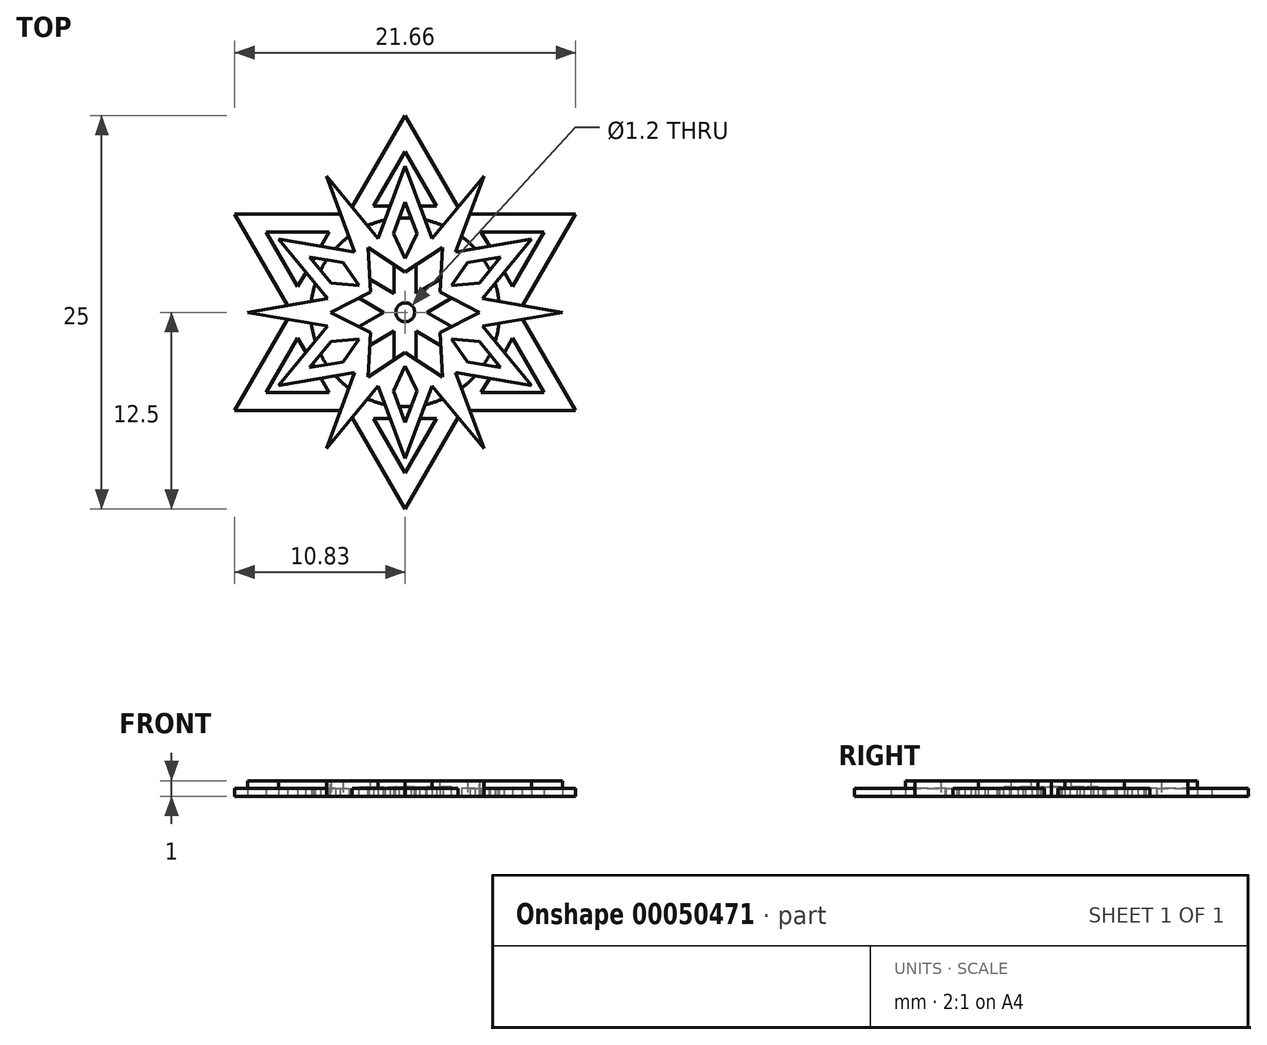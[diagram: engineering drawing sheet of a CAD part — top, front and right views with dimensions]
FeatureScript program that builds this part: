
annotation { "Feature Type Name" : "Feature", "Feature Type Description" : "" }
export const myFeature = defineFeature(function(context is Context, id is Id, definition is map)
    precondition{}
    {
        {
            var Q0;
            Q0=qCreatedBy(makeId("Top.planeOp"),FACE);
            var sketch = newSketch(context, id + "F0", { "sketchPlane" : qUnion([Q0])});
            skCircle(sketch, "E0", {"center": v(0, 0) * mm, "radius": 12.5 * mm, "construction": true});
            skLineSegment(sketch, "E1", {"start": v(0, 12.5) * mm, "end": v(-10.83, -6.25) * mm});
            skLineSegment(sketch, "E2", {"start": v(-10.83, -6.25) * mm, "end": v(10.83, -6.25) * mm});
            skLineSegment(sketch, "E3", {"start": v(10.83, -6.25) * mm, "end": v(0, 12.5) * mm});
            skLineSegment(sketch, "E4", {"start": v(-10.83, 6.25) * mm, "end": v(10.83, 6.25) * mm});
            skLineSegment(sketch, "E5", {"start": v(10.83, 6.25) * mm, "end": v(0, -12.5) * mm});
            skLineSegment(sketch, "E6", {"start": v(0, -12.5) * mm, "end": v(-10.83, 6.25) * mm});
            skCircle(sketch, "E7", {"center": v(0, 0) * mm, "radius": 6 * mm});
            skLineSegment(sketch, "E8", {"start": v(-2, 6.73) * mm, "end": v(2, 6.73) * mm});
            skLineSegment(sketch, "E9", {"start": v(2, 6.73) * mm, "end": v(0, 10.2) * mm});
            skLineSegment(sketch, "E10", {"start": v(0, 10.2) * mm, "end": v(-2, 6.73) * mm});
            skLineSegment(sketch, "E11", {"start": v(0, 10.2) * mm, "end": v(0, 12.5) * mm, "construction": true});
            skLineSegment(sketch, "E12.1.0", {"start": v(-4.83, 5.1) * mm, "end": v(-8.83, 5.1) * mm});
            skLineSegment(sketch, "E12.1.1", {"start": v(-6.83, 1.63) * mm, "end": v(-4.83, 5.1) * mm});
            skLineSegment(sketch, "E12.1.2", {"start": v(-8.83, 5.1) * mm, "end": v(-6.83, 1.63) * mm});
            skLineSegment(sketch, "E12.2.0", {"start": v(-6.83, -1.63) * mm, "end": v(-8.83, -5.1) * mm});
            skLineSegment(sketch, "E12.2.1", {"start": v(-4.83, -5.1) * mm, "end": v(-6.83, -1.63) * mm});
            skLineSegment(sketch, "E12.2.2", {"start": v(-8.83, -5.1) * mm, "end": v(-4.83, -5.1) * mm});
            skLineSegment(sketch, "E12.3.0", {"start": v(-2, -6.73) * mm, "end": v(0, -10.2) * mm});
            skLineSegment(sketch, "E12.3.1", {"start": v(2, -6.73) * mm, "end": v(-2, -6.73) * mm});
            skLineSegment(sketch, "E12.3.2", {"start": v(0, -10.2) * mm, "end": v(2, -6.73) * mm});
            skLineSegment(sketch, "E12.4.0", {"start": v(4.83, -5.1) * mm, "end": v(8.83, -5.1) * mm});
            skLineSegment(sketch, "E12.4.1", {"start": v(6.83, -1.63) * mm, "end": v(4.83, -5.1) * mm});
            skLineSegment(sketch, "E12.4.2", {"start": v(8.83, -5.1) * mm, "end": v(6.83, -1.63) * mm});
            skLineSegment(sketch, "E12.5.0", {"start": v(6.83, 1.63) * mm, "end": v(8.83, 5.1) * mm});
            skLineSegment(sketch, "E12.5.1", {"start": v(4.83, 5.1) * mm, "end": v(6.83, 1.63) * mm});
            skLineSegment(sketch, "E12.5.2", {"start": v(8.83, 5.1) * mm, "end": v(4.83, 5.1) * mm});
            skSolve(sketch);
        }
        {
            var Q0;
            Q0=qSketchRegion(id+"F0",true);
            extrude(context, id + "F1", {"entities" : qUnion([Q0]), "depth" : .5 * mm});
        }
        {
            var Q0;
            Q0=qCreatedBy(makeId("Top.planeOp"),FACE);
            var sketch = newSketch(context, id + "F2", { "sketchPlane" : qUnion([Q0])});
            skArc(sketch, "E13", {"start": v(-1.72, 4.7) * mm, "mid": v(-2.5, 4.33) * mm, "end": v(-3.2, 3.84) * mm});
            skLineSegment(sketch, "E14", {"start": v(-1.72, 4.7) * mm, "end": v(0, 9.28) * mm});
            skLineSegment(sketch, "E15", {"start": v(0, 9.28) * mm, "end": v(1.72, 4.7) * mm});
            skPoint(sketch, "E16.visualSharp", {"position": v(0, 11.28) * mm});
            skPoint(sketch, "E17.orphan", {"position": v(0, 9.28) * mm});
            skLineSegment(sketch, "E18.1.0", {"start": v(-4.93, 0.86) * mm, "end": v(-8.04, 4.64) * mm});
            skLineSegment(sketch, "E18.1.3", {"start": v(-8.04, 4.64) * mm, "end": v(-3.2, 3.84) * mm});
            skLineSegment(sketch, "E18.2.0", {"start": v(-3.2, -3.84) * mm, "end": v(-8.04, -4.64) * mm});
            skLineSegment(sketch, "E18.2.3", {"start": v(-8.04, -4.64) * mm, "end": v(-4.93, -0.86) * mm});
            skLineSegment(sketch, "E18.3.0", {"start": v(1.72, -4.7) * mm, "end": v(0, -9.28) * mm});
            skLineSegment(sketch, "E18.3.3", {"start": v(0, -9.28) * mm, "end": v(-1.72, -4.7) * mm});
            skLineSegment(sketch, "E18.4.0", {"start": v(4.93, -0.86) * mm, "end": v(8.04, -4.64) * mm});
            skLineSegment(sketch, "E18.4.3", {"start": v(8.04, -4.64) * mm, "end": v(3.2, -3.84) * mm});
            skLineSegment(sketch, "E18.5.0", {"start": v(3.2, 3.84) * mm, "end": v(8.04, 4.64) * mm});
            skLineSegment(sketch, "E18.5.3", {"start": v(8.04, 4.64) * mm, "end": v(4.93, 0.86) * mm});
            skArc(sketch, "E19.trimOffspring", {"start": v(3.2, 3.84) * mm, "mid": v(2.5, 4.33) * mm, "end": v(1.72, 4.7) * mm});
            skArc(sketch, "E20.trimOffspring", {"start": v(-4.93, 0.86) * mm, "mid": v(-5, 0) * mm, "end": v(-4.93, -0.86) * mm});
            skArc(sketch, "E21.trimOffspring", {"start": v(4.93, -0.86) * mm, "mid": v(5, 0) * mm, "end": v(4.93, 0.86) * mm});
            skArc(sketch, "E22.trimOffspring", {"start": v(1.72, -4.7) * mm, "mid": v(2.5, -4.33) * mm, "end": v(3.2, -3.84) * mm});
            skArc(sketch, "E23.trimOffspring", {"start": v(-3.2, -3.84) * mm, "mid": v(-2.5, -4.33) * mm, "end": v(-1.72, -4.7) * mm});
            skLineSegment(sketch, "E24", {"start": v(0, 7) * mm, "end": v(0.75, 5) * mm});
            skLineSegment(sketch, "E25", {"start": v(0.75, 5) * mm, "end": v(-0.75, 5) * mm});
            skLineSegment(sketch, "E26", {"start": v(-0.75, 5) * mm, "end": v(0, 7) * mm});
            skLineSegment(sketch, "E27.1.0", {"start": v(-4.7, 1.85) * mm, "end": v(-6.06, 3.5) * mm});
            skLineSegment(sketch, "E27.1.1", {"start": v(-6.06, 3.5) * mm, "end": v(-3.96, 3.15) * mm});
            skLineSegment(sketch, "E27.1.2", {"start": v(-3.96, 3.15) * mm, "end": v(-4.7, 1.85) * mm});
            skLineSegment(sketch, "E27.2.0", {"start": v(-3.96, -3.15) * mm, "end": v(-6.06, -3.5) * mm});
            skLineSegment(sketch, "E27.2.1", {"start": v(-6.06, -3.5) * mm, "end": v(-4.7, -1.85) * mm});
            skLineSegment(sketch, "E27.2.2", {"start": v(-4.7, -1.85) * mm, "end": v(-3.96, -3.15) * mm});
            skLineSegment(sketch, "E27.3.0", {"start": v(0.75, -5) * mm, "end": v(0, -7) * mm});
            skLineSegment(sketch, "E27.3.1", {"start": v(0, -7) * mm, "end": v(-0.75, -5) * mm});
            skLineSegment(sketch, "E27.3.2", {"start": v(-0.75, -5) * mm, "end": v(0.75, -5) * mm});
            skLineSegment(sketch, "E27.4.0", {"start": v(4.7, -1.85) * mm, "end": v(6.06, -3.5) * mm});
            skLineSegment(sketch, "E27.4.1", {"start": v(6.06, -3.5) * mm, "end": v(3.96, -3.15) * mm});
            skLineSegment(sketch, "E27.4.2", {"start": v(3.96, -3.15) * mm, "end": v(4.7, -1.85) * mm});
            skLineSegment(sketch, "E27.5.0", {"start": v(3.96, 3.15) * mm, "end": v(6.06, 3.5) * mm});
            skLineSegment(sketch, "E27.5.1", {"start": v(6.06, 3.5) * mm, "end": v(4.7, 1.85) * mm});
            skLineSegment(sketch, "E27.5.2", {"start": v(4.7, 1.85) * mm, "end": v(3.96, 3.15) * mm});
            skLineSegment(sketch, "E28", {"start": v(0, 9.28) * mm, "end": v(0, 11.28) * mm, "construction": true});
            skLineSegment(sketch, "E29", {"start": v(-3.2, 3.84) * mm, "end": v(-5, 8.66) * mm});
            skLineSegment(sketch, "E30", {"start": v(-5, 8.66) * mm, "end": v(-1.72, 4.7) * mm});
            skLineSegment(sketch, "E31", {"start": v(-5, 8.66) * mm, "end": v(-2.5, 4.33) * mm, "construction": true});
            skLineSegment(sketch, "E32.1.0", {"start": v(-10, 0) * mm, "end": v(-4.93, 0.86) * mm});
            skLineSegment(sketch, "E32.1.1", {"start": v(-4.93, -0.86) * mm, "end": v(-10, 0) * mm});
            skLineSegment(sketch, "E32.2.0", {"start": v(-5, -8.66) * mm, "end": v(-3.2, -3.84) * mm});
            skLineSegment(sketch, "E32.2.1", {"start": v(-1.72, -4.7) * mm, "end": v(-5, -8.66) * mm});
            skLineSegment(sketch, "E32.3.0", {"start": v(5, -8.66) * mm, "end": v(1.72, -4.7) * mm});
            skLineSegment(sketch, "E32.3.1", {"start": v(3.2, -3.84) * mm, "end": v(5, -8.66) * mm});
            skLineSegment(sketch, "E32.4.0", {"start": v(10, 0) * mm, "end": v(4.93, -0.86) * mm});
            skLineSegment(sketch, "E32.4.1", {"start": v(4.93, 0.86) * mm, "end": v(10, 0) * mm});
            skLineSegment(sketch, "E32.5.0", {"start": v(5, 8.66) * mm, "end": v(3.2, 3.84) * mm});
            skLineSegment(sketch, "E32.5.1", {"start": v(1.72, 4.7) * mm, "end": v(5, 8.66) * mm});
            skSolve(sketch);
        }
        {
            var Q0;
            Q0=qSketchRegion(id+"F2",true);
            extrude(context, id + "F3", {"entities" : qUnion([Q0]), "operationType" : NewBodyOperationType.ADD, "depth" : 1 * mm});
        }
        {
            var Q0;
            Q0=makeQuery(id+"F3.opExtrude","CAP_FACE",FACE,{"disambiguationData":[OSD([sQuery(id+"F2.wireOp",EDGE,"E13"),sQuery(id+"F2.wireOp",EDGE,"E14"),sQuery(id+"F2.wireOp",EDGE,"E15"),sQuery(id+"F2.wireOp",EDGE,"1b853f63-bc8d-4a45-9e58-fd6dd771b944"),sQuery(id+"F2.wireOp",EDGE,"199b02c5-8d33-4c38-8ebd-d630f5a1a6e4"),sQuery(id+"F2.wireOp",EDGE,"E16.filletArc"),sQuery(id+"F2.wireOp",EDGE,"E18.1.0"),sQuery(id+"F2.wireOp",EDGE,"E18.1.1"),sQuery(id+"F2.wireOp",EDGE,"E18.1.2"),sQuery(id+"F2.wireOp",EDGE,"E18.1.3"),sQuery(id+"F2.wireOp",EDGE,"E18.1.4"),sQuery(id+"F2.wireOp",EDGE,"E18.2.0"),sQuery(id+"F2.wireOp",EDGE,"E18.2.1"),sQuery(id+"F2.wireOp",EDGE,"E18.2.2"),sQuery(id+"F2.wireOp",EDGE,"E18.2.3"),sQuery(id+"F2.wireOp",EDGE,"E18.2.4"),sQuery(id+"F2.wireOp",EDGE,"E18.3.0"),sQuery(id+"F2.wireOp",EDGE,"E18.3.1"),sQuery(id+"F2.wireOp",EDGE,"E18.3.2"),sQuery(id+"F2.wireOp",EDGE,"E18.3.3"),sQuery(id+"F2.wireOp",EDGE,"E18.3.4"),sQuery(id+"F2.wireOp",EDGE,"E18.4.0"),sQuery(id+"F2.wireOp",EDGE,"E18.4.1"),sQuery(id+"F2.wireOp",EDGE,"E18.4.2"),sQuery(id+"F2.wireOp",EDGE,"E18.4.3"),sQuery(id+"F2.wireOp",EDGE,"E18.4.4"),sQuery(id+"F2.wireOp",EDGE,"E18.5.0"),sQuery(id+"F2.wireOp",EDGE,"E18.5.1"),sQuery(id+"F2.wireOp",EDGE,"E18.5.2"),sQuery(id+"F2.wireOp",EDGE,"E18.5.3"),sQuery(id+"F2.wireOp",EDGE,"E18.5.4"),sQuery(id+"F2.wireOp",EDGE,"E19.trimOffspring"),sQuery(id+"F2.wireOp",EDGE,"E20.trimOffspring"),sQuery(id+"F2.wireOp",EDGE,"E21.trimOffspring"),sQuery(id+"F2.wireOp",EDGE,"E22.trimOffspring"),sQuery(id+"F2.wireOp",EDGE,"E23.trimOffspring"),sQuery(id+"F2.wireOp",EDGE,"E24"),sQuery(id+"F2.wireOp",EDGE,"E25"),sQuery(id+"F2.wireOp",EDGE,"E26"),sQuery(id+"F2.wireOp",EDGE,"E27.1.0"),sQuery(id+"F2.wireOp",EDGE,"E27.1.1"),sQuery(id+"F2.wireOp",EDGE,"E27.1.2"),sQuery(id+"F2.wireOp",EDGE,"E27.2.0"),sQuery(id+"F2.wireOp",EDGE,"E27.2.1"),sQuery(id+"F2.wireOp",EDGE,"E27.2.2"),sQuery(id+"F2.wireOp",EDGE,"E27.3.0"),sQuery(id+"F2.wireOp",EDGE,"E27.3.1"),sQuery(id+"F2.wireOp",EDGE,"E27.3.2"),sQuery(id+"F2.wireOp",EDGE,"E27.4.0"),sQuery(id+"F2.wireOp",EDGE,"E27.4.1"),sQuery(id+"F2.wireOp",EDGE,"E27.4.2"),sQuery(id+"F2.wireOp",EDGE,"E27.5.0"),sQuery(id+"F2.wireOp",EDGE,"E27.5.1"),sQuery(id+"F2.wireOp",EDGE,"E27.5.2")])],"isStart":false});
            var sketch = newSketch(context, id + "F4", { "sketchPlane" : qUnion([Q0])});
            skLineSegment(sketch, "E33", {"start": v(-0.75, 5) * mm, "end": v(0.75, 5) * mm});
            skLineSegment(sketch, "E34", {"start": v(0.75, 5) * mm, "end": v(0, 3.4) * mm});
            skLineSegment(sketch, "E35", {"start": v(0, 3.4) * mm, "end": v(-0.75, 5) * mm});
            skLineSegment(sketch, "E36", {"start": v(0.7, 3) * mm, "end": v(0.7, 1.2) * mm});
            skLineSegment(sketch, "E37", {"start": v(0.7, 1.2) * mm, "end": v(2.25, 2.1) * mm});
            skLineSegment(sketch, "E38", {"start": v(2.25, 2.1) * mm, "end": v(2.37, 4.1) * mm});
            skLineSegment(sketch, "E39", {"start": v(2.37, 4.1) * mm, "end": v(0.7, 3) * mm});
            skLineSegment(sketch, "E40", {"start": v(0, 0) * mm, "end": v(2.37, 4.1) * mm, "construction": true});
            skLineSegment(sketch, "E41", {"start": v(2.95, 0) * mm, "end": v(0, 0) * mm, "construction": true});
            skLineSegment(sketch, "E42", {"start": v(0, 3.4) * mm, "end": v(0.7, 3) * mm, "construction": true});
            skLineSegment(sketch, "E43.1.0", {"start": v(-3.96, 3.15) * mm, "end": v(-2.94, 1.7) * mm});
            skLineSegment(sketch, "E43.1.1", {"start": v(-2.94, 1.7) * mm, "end": v(-4.7, 1.85) * mm});
            skLineSegment(sketch, "E43.1.2", {"start": v(-4.7, 1.85) * mm, "end": v(-3.96, 3.15) * mm});
            skLineSegment(sketch, "E43.1.3", {"start": v(-2.37, 4.1) * mm, "end": v(-2.25, 2.1) * mm});
            skLineSegment(sketch, "E43.1.4", {"start": v(-2.25, 2.1) * mm, "end": v(-0.7, 1.2) * mm});
            skLineSegment(sketch, "E43.1.5", {"start": v(-0.7, 1.2) * mm, "end": v(-0.7, 3) * mm});
            skLineSegment(sketch, "E43.1.6", {"start": v(-0.7, 3) * mm, "end": v(-2.37, 4.1) * mm});
            skLineSegment(sketch, "E43.2.0", {"start": v(-4.7, -1.85) * mm, "end": v(-2.94, -1.7) * mm});
            skLineSegment(sketch, "E43.2.1", {"start": v(-2.94, -1.7) * mm, "end": v(-3.96, -3.15) * mm});
            skLineSegment(sketch, "E43.2.2", {"start": v(-3.96, -3.15) * mm, "end": v(-4.7, -1.85) * mm});
            skLineSegment(sketch, "E43.2.3", {"start": v(-4.73, 0) * mm, "end": v(-2.94, -0.9) * mm});
            skLineSegment(sketch, "E43.2.4", {"start": v(-2.94, -0.9) * mm, "end": v(-1.39, 0) * mm});
            skLineSegment(sketch, "E43.2.5", {"start": v(-1.39, 0) * mm, "end": v(-2.94, 0.9) * mm});
            skLineSegment(sketch, "E43.2.6", {"start": v(-2.94, 0.9) * mm, "end": v(-4.73, 0) * mm});
            skLineSegment(sketch, "E43.3.0", {"start": v(-0.75, -5) * mm, "end": v(0, -3.4) * mm});
            skLineSegment(sketch, "E43.3.1", {"start": v(0, -3.4) * mm, "end": v(0.75, -5) * mm});
            skLineSegment(sketch, "E43.3.2", {"start": v(0.75, -5) * mm, "end": v(-0.75, -5) * mm});
            skLineSegment(sketch, "E43.3.3", {"start": v(-2.37, -4.1) * mm, "end": v(-0.7, -3) * mm});
            skLineSegment(sketch, "E43.3.4", {"start": v(-0.7, -3) * mm, "end": v(-0.7, -1.2) * mm});
            skLineSegment(sketch, "E43.3.5", {"start": v(-0.7, -1.2) * mm, "end": v(-2.25, -2.1) * mm});
            skLineSegment(sketch, "E43.3.6", {"start": v(-2.25, -2.1) * mm, "end": v(-2.37, -4.1) * mm});
            skLineSegment(sketch, "E43.4.0", {"start": v(3.96, -3.15) * mm, "end": v(2.94, -1.7) * mm});
            skLineSegment(sketch, "E43.4.1", {"start": v(2.94, -1.7) * mm, "end": v(4.7, -1.85) * mm});
            skLineSegment(sketch, "E43.4.2", {"start": v(4.7, -1.85) * mm, "end": v(3.96, -3.15) * mm});
            skLineSegment(sketch, "E43.4.3", {"start": v(2.37, -4.1) * mm, "end": v(2.25, -2.1) * mm});
            skLineSegment(sketch, "E43.4.4", {"start": v(2.25, -2.1) * mm, "end": v(0.7, -1.2) * mm});
            skLineSegment(sketch, "E43.4.5", {"start": v(0.7, -1.2) * mm, "end": v(0.7, -3) * mm});
            skLineSegment(sketch, "E43.4.6", {"start": v(0.7, -3) * mm, "end": v(2.37, -4.1) * mm});
            skLineSegment(sketch, "E43.5.0", {"start": v(4.7, 1.85) * mm, "end": v(2.94, 1.7) * mm});
            skLineSegment(sketch, "E43.5.1", {"start": v(2.94, 1.7) * mm, "end": v(3.96, 3.15) * mm});
            skLineSegment(sketch, "E43.5.2", {"start": v(3.96, 3.15) * mm, "end": v(4.7, 1.85) * mm});
            skLineSegment(sketch, "E43.5.3", {"start": v(4.73, 0) * mm, "end": v(2.94, 0.9) * mm});
            skLineSegment(sketch, "E43.5.4", {"start": v(2.94, 0.9) * mm, "end": v(1.39, 0) * mm});
            skLineSegment(sketch, "E43.5.5", {"start": v(1.39, 0) * mm, "end": v(2.94, -0.9) * mm});
            skLineSegment(sketch, "E43.5.6", {"start": v(2.94, -0.9) * mm, "end": v(4.73, 0) * mm});
            skPoint(sketch, "E43.center", {"position": v(0, 0) * mm});
            skCircle(sketch, "E44", {"center": v(0, 0) * mm, "radius": 0.6 * mm});
            skSolve(sketch);
        }
        {
            var Q0;
            Q0 = qSketchRegion(id + "F4", true);
            extrude(context, id + "F5", {"entities" : qUnion([Q0]), "operationType" : NewBodyOperationType.REMOVE, "oppositeDirection" : true, "depth" : 25 * mm});
        }
        {
            var Q0;
            Q0=makeQuery(id+"F3.opExtrude","CAP_FACE",FACE,{"disambiguationData":[OSD([sQuery(id+"F2.wireOp",EDGE,"E14"),sQuery(id+"F2.wireOp",EDGE,"E15"),sQuery(id+"F2.wireOp",EDGE,"E18.1.0"),sQuery(id+"F2.wireOp",EDGE,"E18.1.3"),sQuery(id+"F2.wireOp",EDGE,"E18.2.0"),sQuery(id+"F2.wireOp",EDGE,"E18.2.3"),sQuery(id+"F2.wireOp",EDGE,"E18.3.0"),sQuery(id+"F2.wireOp",EDGE,"E18.3.3"),sQuery(id+"F2.wireOp",EDGE,"E18.4.0"),sQuery(id+"F2.wireOp",EDGE,"E18.4.3"),sQuery(id+"F2.wireOp",EDGE,"E18.5.0"),sQuery(id+"F2.wireOp",EDGE,"E18.5.3"),sQuery(id+"F2.wireOp",EDGE,"E24"),sQuery(id+"F2.wireOp",EDGE,"E25"),sQuery(id+"F2.wireOp",EDGE,"E26"),sQuery(id+"F2.wireOp",EDGE,"E27.1.0"),sQuery(id+"F2.wireOp",EDGE,"E27.1.1"),sQuery(id+"F2.wireOp",EDGE,"E27.1.2"),sQuery(id+"F2.wireOp",EDGE,"E27.2.0"),sQuery(id+"F2.wireOp",EDGE,"E27.2.1"),sQuery(id+"F2.wireOp",EDGE,"E27.2.2"),sQuery(id+"F2.wireOp",EDGE,"E27.3.0"),sQuery(id+"F2.wireOp",EDGE,"E27.3.1"),sQuery(id+"F2.wireOp",EDGE,"E27.3.2"),sQuery(id+"F2.wireOp",EDGE,"E27.4.0"),sQuery(id+"F2.wireOp",EDGE,"E27.4.1"),sQuery(id+"F2.wireOp",EDGE,"E27.4.2"),sQuery(id+"F2.wireOp",EDGE,"E27.5.0"),sQuery(id+"F2.wireOp",EDGE,"E27.5.1"),sQuery(id+"F2.wireOp",EDGE,"E27.5.2"),sQuery(id+"F2.wireOp",EDGE,"E29"),sQuery(id+"F2.wireOp",EDGE,"E30"),sQuery(id+"F2.wireOp",EDGE,"E32.1.0"),sQuery(id+"F2.wireOp",EDGE,"E32.1.1"),sQuery(id+"F2.wireOp",EDGE,"E32.2.0"),sQuery(id+"F2.wireOp",EDGE,"E32.2.1"),sQuery(id+"F2.wireOp",EDGE,"E32.3.0"),sQuery(id+"F2.wireOp",EDGE,"E32.3.1"),sQuery(id+"F2.wireOp",EDGE,"E32.4.0"),sQuery(id+"F2.wireOp",EDGE,"E32.4.1"),sQuery(id+"F2.wireOp",EDGE,"E32.5.0"),sQuery(id+"F2.wireOp",EDGE,"E32.5.1")])],"isStart":false});
            var sketch = newSketch(context, id + "F6", { "sketchPlane" : qUnion([Q0])});
            skLineSegment(sketch, "E45", {"start": v(-0.7, 3) * mm, "end": v(0, 2.55) * mm});
            skLineSegment(sketch, "E46", {"start": v(0, 2.55) * mm, "end": v(0.7, 3) * mm});
            skLineSegment(sketch, "E47", {"start": v(2.25, 2.1) * mm, "end": v(2.2, 1.27) * mm});
            skLineSegment(sketch, "E48", {"start": v(2.2, 1.27) * mm, "end": v(2.94, 0.9) * mm});
            skLineSegment(sketch, "E49", {"start": v(2.94, -0.9) * mm, "end": v(2.2, -1.27) * mm});
            skLineSegment(sketch, "E50", {"start": v(2.2, -1.27) * mm, "end": v(2.25, -2.1) * mm});
            skLineSegment(sketch, "E51", {"start": v(0.7, -3) * mm, "end": v(0, -2.55) * mm});
            skLineSegment(sketch, "E52", {"start": v(0, -2.55) * mm, "end": v(-0.7, -3) * mm});
            skLineSegment(sketch, "E53", {"start": v(-2.25, -2.1) * mm, "end": v(-2.2, -1.27) * mm});
            skLineSegment(sketch, "E54", {"start": v(-2.2, -1.27) * mm, "end": v(-2.94, -0.9) * mm});
            skLineSegment(sketch, "E55", {"start": v(-2.94, 0.9) * mm, "end": v(-2.2, 1.27) * mm});
            skLineSegment(sketch, "E56", {"start": v(-2.2, 1.27) * mm, "end": v(-2.25, 2.1) * mm});
            skLineSegment(sketch, "E57", {"start": v(-2.25, 2.1) * mm, "end": v(-0.7, 1.2) * mm});
            skLineSegment(sketch, "E58", {"start": v(-0.7, 1.2) * mm, "end": v(-0.7, 3) * mm});
            skLineSegment(sketch, "E59", {"start": v(0.7, 3) * mm, "end": v(0.7, 1.2) * mm});
            skLineSegment(sketch, "E60", {"start": v(0.7, 1.2) * mm, "end": v(2.25, 2.1) * mm});
            skLineSegment(sketch, "E61", {"start": v(2.94, 0.9) * mm, "end": v(1.39, 0) * mm});
            skLineSegment(sketch, "E62", {"start": v(1.39, 0) * mm, "end": v(2.94, -0.9) * mm});
            skLineSegment(sketch, "E63", {"start": v(2.25, -2.1) * mm, "end": v(0.7, -1.2) * mm});
            skLineSegment(sketch, "E64", {"start": v(0.7, -1.2) * mm, "end": v(0.7, -3) * mm});
            skLineSegment(sketch, "E65", {"start": v(-0.7, -3) * mm, "end": v(-0.7, -1.2) * mm});
            skLineSegment(sketch, "E66", {"start": v(-0.7, -1.2) * mm, "end": v(-2.25, -2.1) * mm});
            skLineSegment(sketch, "E67", {"start": v(-2.94, -0.9) * mm, "end": v(-1.39, 0) * mm});
            skLineSegment(sketch, "E68", {"start": v(-1.39, 0) * mm, "end": v(-2.94, 0.9) * mm});
            skSolve(sketch);
        }
        {
            var Q0;
            Q0 = qSketchRegion(id + "F6", true);
            extrude(context, id + "F7", {"entities" : qUnion([Q0]), "operationType" : NewBodyOperationType.REMOVE, "oppositeDirection" : true, "depth" : 0.4 * mm});
        }
    });
